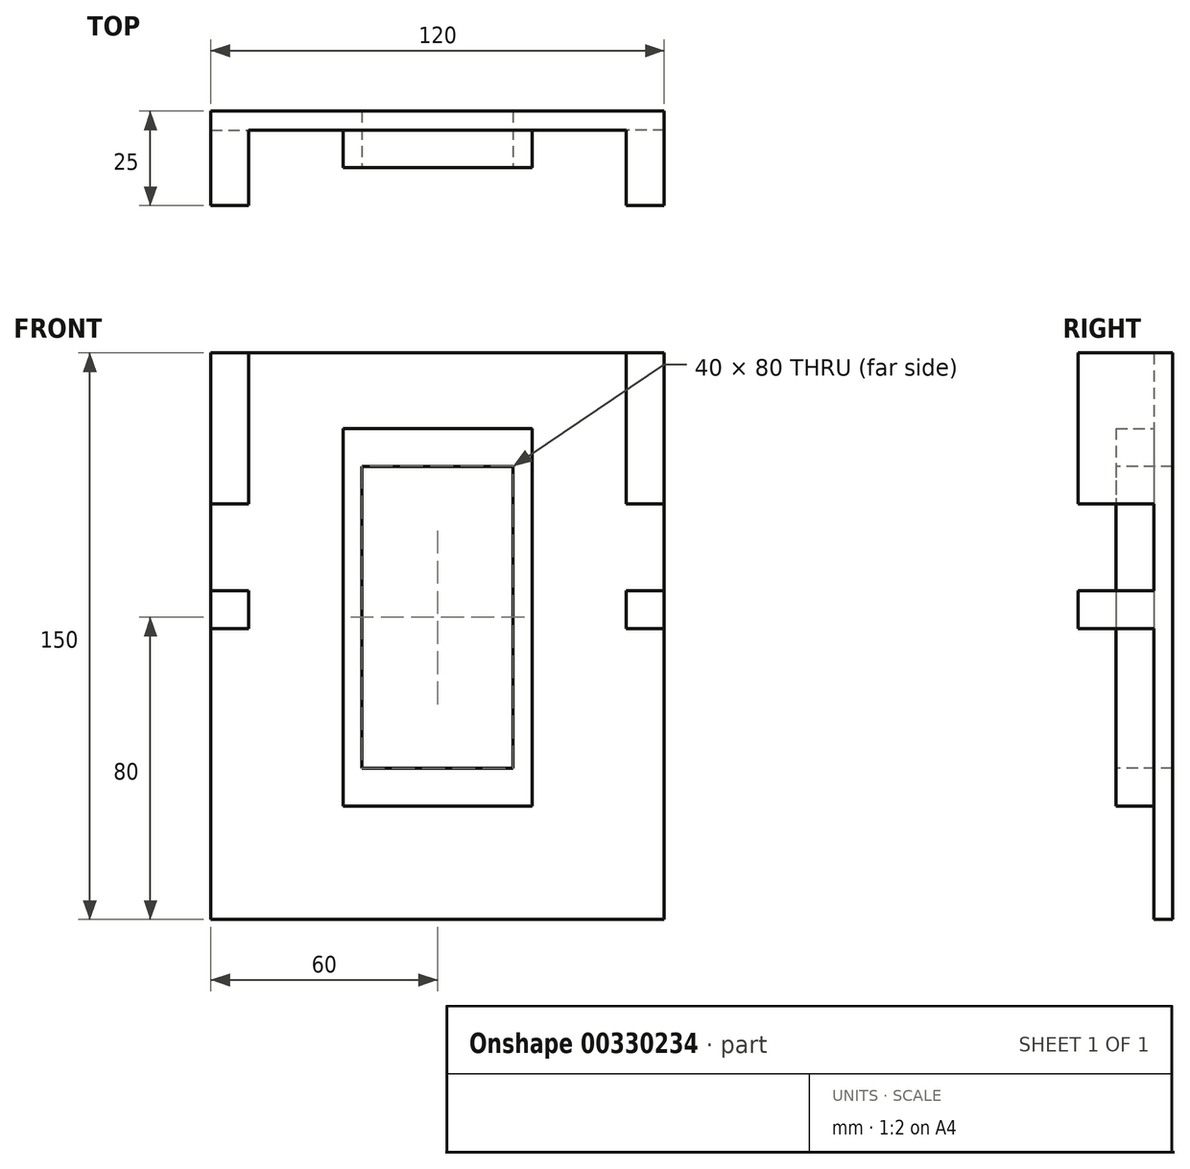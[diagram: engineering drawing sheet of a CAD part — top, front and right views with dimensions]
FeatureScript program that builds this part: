
annotation { "Feature Type Name" : "Feature", "Feature Type Description" : "" }
export const myFeature = defineFeature(function(context is Context, id is Id, definition is map)
    precondition{}
    {
        {
            var Q0;
            Q0=qCreatedBy(makeId("Front.planeOp"),FACE);
            var sketch = newSketch(context, id + "F0", { "sketchPlane" : qUnion([Q0])});
            skLineSegment(sketch, "E0.bottom", {"start": v(-60, 60) * mm, "end": v(60, 60) * mm});
            skLineSegment(sketch, "E0.top", {"start": v(-60, -90) * mm, "end": v(60, -90) * mm});
            skLineSegment(sketch, "E0.left", {"start": v(-60, 60) * mm, "end": v(-60, -90) * mm});
            skLineSegment(sketch, "E0.right", {"start": v(60, 60) * mm, "end": v(60, -90) * mm});
            skSolve(sketch);
        }
        {
            var Q0;
            Q0 = qSketchRegion(id + "F0", true);
            extrude(context, id + "F1", {"entities" : qUnion([Q0]), "depth" : 5 * mm});
        }
        {
            var Q0;
            Q0=makeQuery(id+"F1.opExtrude","CAP_FACE",FACE,{"disambiguationData":[OSD([sQuery(id+"F0.wireOp",EDGE,"E0.bottom"),sQuery(id+"F0.wireOp",EDGE,"E0.top"),sQuery(id+"F0.wireOp",EDGE,"E0.left"),sQuery(id+"F0.wireOp",EDGE,"E0.right")])],"isStart":false});
            var sketch = newSketch(context, id + "F2", { "sketchPlane" : qUnion([Q0])});
            skLineSegment(sketch, "E1.bottom", {"start": v(-20, 30) * mm, "end": v(20, 30) * mm});
            skLineSegment(sketch, "E1.top", {"start": v(-20, -50) * mm, "end": v(20, -50) * mm});
            skLineSegment(sketch, "E1.left", {"start": v(-20, 30) * mm, "end": v(-20, -50) * mm});
            skLineSegment(sketch, "E1.right", {"start": v(20, 30) * mm, "end": v(20, -50) * mm});
            skSolve(sketch);
        }
        {
            var Q0;
            Q0 = qSketchRegion(id + "F2", true);
            extrude(context, id + "F3", {"entities" : qUnion([Q0]), "operationType" : NewBodyOperationType.REMOVE, "endBound" : BoundingType.THROUGH_ALL, "oppositeDirection" : true, "depth" : 25 * mm});
        }
        {
            var Q0;
            Q0=makeQuery(id+"F1.opExtrude","CAP_FACE",FACE,{"disambiguationData":[OSD([sQuery(id+"F0.wireOp",EDGE,"E0.bottom"),sQuery(id+"F0.wireOp",EDGE,"E0.top"),sQuery(id+"F0.wireOp",EDGE,"E0.left"),sQuery(id+"F0.wireOp",EDGE,"E0.right")])],"isStart":false});
            var sketch = newSketch(context, id + "F4", { "sketchPlane" : qUnion([Q0])});
            skLineSegment(sketch, "E2.bottom", {"start": v(-60, 60) * mm, "end": v(-50, 60) * mm});
            skLineSegment(sketch, "E2.top", {"start": v(-60, 20) * mm, "end": v(-50, 20) * mm});
            skLineSegment(sketch, "E2.left", {"start": v(-60, 60) * mm, "end": v(-60, 20) * mm});
            skLineSegment(sketch, "E2.right", {"start": v(-50, 60) * mm, "end": v(-50, 20) * mm});
            skLineSegment(sketch, "E3.bottom", {"start": v(-60, -3) * mm, "end": v(-50, -3) * mm});
            skLineSegment(sketch, "E3.top", {"start": v(-60, -13) * mm, "end": v(-50, -13) * mm});
            skLineSegment(sketch, "E3.left", {"start": v(-60, -3) * mm, "end": v(-60, -13) * mm});
            skLineSegment(sketch, "E3.right", {"start": v(-50, -3) * mm, "end": v(-50, -13) * mm});
            skLineSegment(sketch, "E4.bottom", {"start": v(60, 60) * mm, "end": v(50, 60) * mm});
            skLineSegment(sketch, "E4.top", {"start": v(60, 20) * mm, "end": v(50, 20) * mm});
            skLineSegment(sketch, "E4.left", {"start": v(60, 60) * mm, "end": v(60, 20) * mm});
            skLineSegment(sketch, "E4.right", {"start": v(50, 60) * mm, "end": v(50, 20) * mm});
            skLineSegment(sketch, "E5.bottom", {"start": v(60, -3) * mm, "end": v(50, -3) * mm});
            skLineSegment(sketch, "E5.top", {"start": v(60, -13) * mm, "end": v(50, -13) * mm});
            skLineSegment(sketch, "E5.left", {"start": v(60, -3) * mm, "end": v(60, -13) * mm});
            skLineSegment(sketch, "E5.right", {"start": v(50, -3) * mm, "end": v(50, -13) * mm});
            skSolve(sketch);
        }
        {
            var Q0;
            Q0 = qSketchRegion(id + "F4", true);
            extrude(context, id + "F5", {"entities" : qUnion([Q0]), "operationType" : NewBodyOperationType.ADD, "depth" : 20 * mm});
        }
        {
            var Q0;
            Q0=makeQuery(id+"F1.opExtrude","CAP_FACE",FACE,{"disambiguationData":[OSD([sQuery(id+"F0.wireOp",EDGE,"E0.bottom"),sQuery(id+"F0.wireOp",EDGE,"E0.top"),sQuery(id+"F0.wireOp",EDGE,"E0.left"),sQuery(id+"F0.wireOp",EDGE,"E0.right")])],"isStart":false});
            var sketch = newSketch(context, id + "F6", { "sketchPlane" : qUnion([Q0])});
            skLineSegment(sketch, "E6.bottom", {"start": v(-20, 30) * mm, "end": v(20, 30) * mm});
            skLineSegment(sketch, "E6.top", {"start": v(-20, 40) * mm, "end": v(20, 40) * mm});
            skLineSegment(sketch, "E6.left", {"start": v(-20, 30) * mm, "end": v(-20, 40) * mm});
            skLineSegment(sketch, "E6.right", {"start": v(20, 30) * mm, "end": v(20, 40) * mm});
            skLineSegment(sketch, "E7.bottom", {"start": v(-20, -50) * mm, "end": v(20, -50) * mm});
            skLineSegment(sketch, "E7.top", {"start": v(-20, -60) * mm, "end": v(20, -60) * mm});
            skLineSegment(sketch, "E7.left", {"start": v(-20, -50) * mm, "end": v(-20, -60) * mm});
            skLineSegment(sketch, "E7.right", {"start": v(20, -50) * mm, "end": v(20, -60) * mm});
            skLineSegment(sketch, "E8.bottom", {"start": v(-20, 40) * mm, "end": v(-25, 40) * mm});
            skLineSegment(sketch, "E8.top", {"start": v(-20, -60) * mm, "end": v(-25, -60) * mm});
            skLineSegment(sketch, "E8.left", {"start": v(-20, 40) * mm, "end": v(-20, -60) * mm});
            skLineSegment(sketch, "E8.right", {"start": v(-25, 40) * mm, "end": v(-25, -60) * mm});
            skLineSegment(sketch, "E9.bottom", {"start": v(20, 40) * mm, "end": v(25, 40) * mm});
            skLineSegment(sketch, "E9.top", {"start": v(20, -60) * mm, "end": v(25, -60) * mm});
            skLineSegment(sketch, "E9.left", {"start": v(20, 40) * mm, "end": v(20, -60) * mm});
            skLineSegment(sketch, "E9.right", {"start": v(25, 40) * mm, "end": v(25, -60) * mm});
            skSolve(sketch);
        }
        {
            var Q0;
            Q0 = qSketchRegion(id + "F6", true);
            extrude(context, id + "F7", {"entities" : qUnion([Q0]), "operationType" : NewBodyOperationType.ADD, "depth" : 10 * mm});
        }
    });
